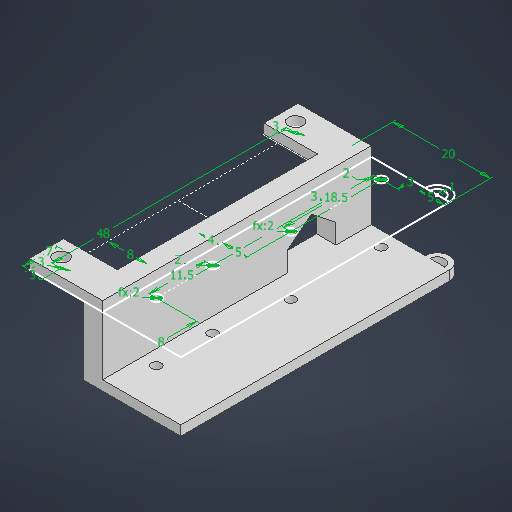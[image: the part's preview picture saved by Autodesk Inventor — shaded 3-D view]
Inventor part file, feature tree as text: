
AUTODESK INVENTOR PART (.ipt)
format: ipt  version: 2025.1 (Build 291241000, 241)  size: 524,800 bytes
history: native  units: mm
features: extrude x4, sketch x2, chamfer x1, projected_geometry x1
ambient origin geometry x8: Origin, YZ Plane, XZ Plane, XY Plane, X Axis, Y Axis, Z Axis, Center Point
bodies: Solid1 (feature_tree)
feature tree (8):
  sketch  "Sketch1"  dims[d0=3.0mm d1=3.0mm]
  extrude  "Extrusion1"  Depth=3.0mm
  extrude  "Extrusion2"  Depth=7.0mm
  extrude  "Extrusion3"  Depth=48.0mm
  extrude  "Extrusion4"  Depth=4.0mm
  chamfer  "Chamfer1"  Distance=4.0mm
  sketch  "Sketch2"  dims[d2=3.0mm d3=7.0mm d4=48.0mm d5=8.0mm d7=4.0mm d8=2.0mm d9=0.0mm d10=14.0mm d11=0.0mm d12=20.0mm d13=2.0mm d14=2.0mm d15=11.5mm d16=3.0mm d17=2.0mm d18=2.0mm d19=18.5mm d20=5.0mm d23=8.0mm d24=3.0mm d25=2.0mm d26=0.0mm d27=5.0mm d28=1.0mm d29=10.0mm d30=8.0mm d31=0.0mm d32=0.0mm d33=5.0mm d34=4.0mm d35=45.0deg]
  projected_geometry  "Projected Loop1"
